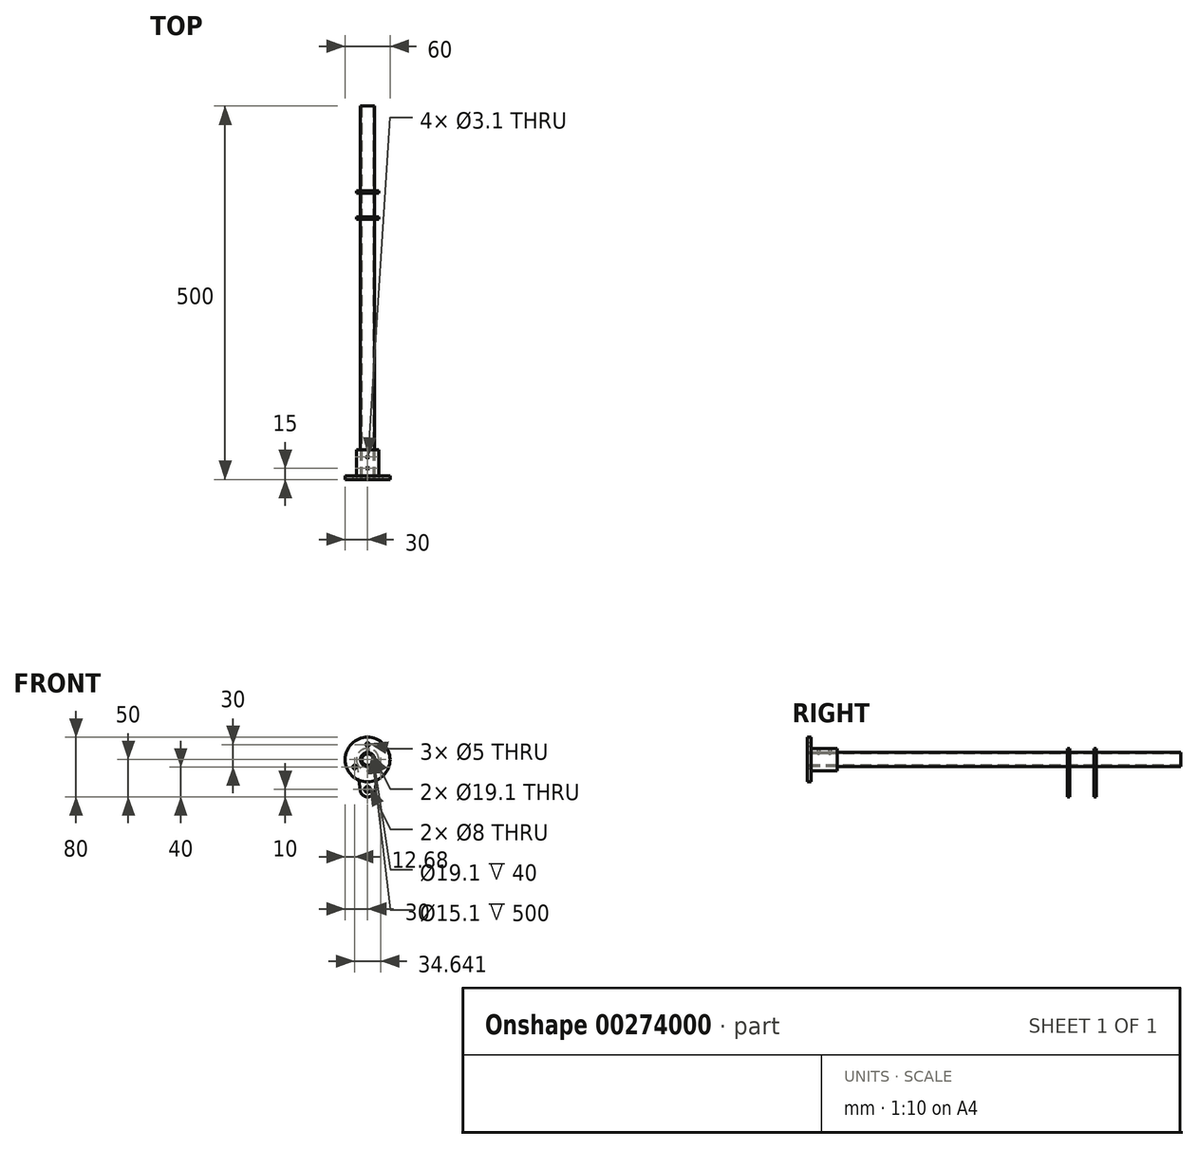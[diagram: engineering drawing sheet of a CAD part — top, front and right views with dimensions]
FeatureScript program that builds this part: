
annotation { "Feature Type Name" : "Feature", "Feature Type Description" : "" }
export const myFeature = defineFeature(function(context is Context, id is Id, definition is map)
    precondition{}
    {
        {
            var Q0;
            Q0=qCreatedBy(makeId("Front.planeOp"),FACE);
            var sketch = newSketch(context, id + "F0", { "sketchPlane" : qUnion([Q0])});
            skCircle(sketch, "E0", {"center": v(0, 0) * mm, "radius": 9.55 * mm});
            skCircle(sketch, "E1", {"center": v(0, 0) * mm, "radius": 7.55 * mm});
            skSolve(sketch);
        }
        {
            var Q0;
            Q0=qSketchRegion(id+"F0",true);
            extrude(context, id + "F1", {"entities" : qUnion([Q0]), "oppositeDirection" : true, "depth" : 500 * mm});
        }
        {
            var Q0;
            Q0=qCreatedBy(makeId("Right.planeOp"),FACE);
            var sketch = newSketch(context, id + "F2", { "sketchPlane" : qUnion([Q0])});
            skLineSegment(sketch, "E2", {"start": v(0, -9.55) * mm, "end": v(500, -9.55) * mm, "construction": true});
            skLineSegment(sketch, "E3", {"start": v(500, 9.55) * mm, "end": v(0, 9.55) * mm, "construction": true});
            skLineSegment(sketch, "E4", {"start": v(0, 9.55) * mm, "end": v(0, -9.55) * mm, "construction": true});
            skLineSegment(sketch, "E5", {"start": v(0, 0) * mm, "end": v(72.27, 0) * mm, "construction": true});
            skLineSegment(sketch, "E6", {"start": v(0, 9.55) * mm, "end": v(0, 30) * mm});
            skLineSegment(sketch, "E7", {"start": v(0, 30) * mm, "end": v(5, 30) * mm});
            skLineSegment(sketch, "E8", {"start": v(5, 30) * mm, "end": v(5, 15) * mm});
            skLineSegment(sketch, "E9", {"start": v(5, 15) * mm, "end": v(40, 15) * mm});
            skLineSegment(sketch, "E10", {"start": v(40, 15) * mm, "end": v(40, 9.55) * mm});
            skLineSegment(sketch, "E11", {"start": v(40, 9.55) * mm, "end": v(0, 9.55) * mm});
            skSolve(sketch);
        }
        {
            var Q0;
            Q0=qSketchRegion(id+"F2",true);
            var Q1;
            Q1=sQuery(id+"F2.wireOp",EDGE,"E5");
            revolve(context, id + "F3", {"entities" : qUnion([Q0]), "axis" : qUnion([Q1]), "revolveType" : RevolveType.FULL});
        }
        {
            var Q0;
            Q0=makeQuery(id+"F3.opRevolve","SWEPT_FACE",FACE,{"disambiguationData":[OSD([sQuery(id+"F2.wireOp",EDGE,"E6")])]});
            var sketch = newSketch(context, id + "F4", { "sketchPlane" : qUnion([Q0])});
            skCircle(sketch, "E12", {"center": v(0, 0) * mm, "radius": 20 * mm, "construction": true});
            skCircle(sketch, "E13", {"center": v(0, 20) * mm, "radius": 2.5 * mm});
            skCircle(sketch, "E14.1.0", {"center": v(-17.32, -10) * mm, "radius": 2.5 * mm});
            skCircle(sketch, "E14.2.0", {"center": v(17.32, -10) * mm, "radius": 2.5 * mm});
            skSolve(sketch);
        }
        {
            var Q0;
            Q0=qSketchRegion(id+"F4",true);
            extrude(context, id + "F5", {"entities" : qUnion([Q0]), "operationType" : NewBodyOperationType.REMOVE, "endBound" : BoundingType.THROUGH_ALL, "oppositeDirection" : true, "depth" : 25 * mm});
        }
        {
            var Q0;
            Q0=qCreatedBy(makeId("Top.planeOp"),FACE);
            var sketch = newSketch(context, id + "F6", { "sketchPlane" : qUnion([Q0])});
            skLineSegment(sketch, "E15", {"start": v(0, 0) * mm, "end": v(0, 30) * mm, "construction": true});
            skCircle(sketch, "E16", {"center": v(0, 30) * mm, "radius": 1.55 * mm});
            skCircle(sketch, "E17", {"center": v(0, 15) * mm, "radius": 1.55 * mm});
            skSolve(sketch);
        }
        {
            var Q0;
            Q0=qSketchRegion(id+"F6",true);
            extrude(context, id + "F7", {"entities" : qUnion([Q0]), "operationType" : NewBodyOperationType.REMOVE, "endBound" : BoundingType.THROUGH_ALL, "depth" : 25 * mm});
        }
        {
            var Q0;
            Q0=makeQuery(id+"F1.opExtrude","CAP_FACE",FACE,{"disambiguationData":[OSD([sQuery(id+"F0.wireOp",EDGE,"E0"),sQuery(id+"F0.wireOp",EDGE,"E1")])],"isStart":false});
            cPlane(context, id + "F8", {"entities" : qUnion([Q0]), "cplaneType" : CPlaneType.OFFSET, "offset" : 150 * mm, "oppositeDirection" : true, "width" : 150 * mm, "height" : 150 * mm});
        }
        {
            var Q0;
            Q0=qCreatedBy(id+"F8.planeOp",FACE);
            var sketch = newSketch(context, id + "F9", { "sketchPlane" : qUnion([Q0])});
            skCircle(sketch, "E18.0", {"center": v(0, 0) * mm, "radius": 9.55 * mm});
            skArc(sketch, "E19.0", {"start": v(14.88, -1.87) * mm, "mid": v(0, 15) * mm, "end": v(-14.88, -1.87) * mm});
            skLineSegment(sketch, "E20", {"start": v(0, 0) * mm, "end": v(0, -40) * mm, "construction": true});
            skArc(sketch, "E21", {"start": v(-9.92, -41.25) * mm, "mid": v(0, -50) * mm, "end": v(9.92, -41.25) * mm});
            skLineSegment(sketch, "E22", {"start": v(-14.88, -1.87) * mm, "end": v(-9.92, -41.25) * mm});
            skLineSegment(sketch, "E23", {"start": v(14.88, -1.87) * mm, "end": v(9.92, -41.25) * mm});
            skCircle(sketch, "E24", {"center": v(0, -40) * mm, "radius": 4 * mm});
            skSolve(sketch);
        }
        {
            var Q0;
            Q0=makeQuery(id+"F9.imprint","IMPRINT",FACE,{"disambiguationData":[TD([[makeQuery(id+"F9.imprint","IMPRINT",EDGE,{"derivedFrom":sQuery(id+"F9.wireOp",EDGE,"E18.0")}),-1.0]])]});
            extrude(context, id + "F10", {"entities" : qUnion([Q0]), "endBound" : BoundingType.SYMMETRIC, "depth" : 3.2 * mm});
        }
        {
            var Q0;
            Q0=makeQuery(id+"F10.opExtrude","SWEPT_BODY",BODY,{"disambiguationData":[OSD([sQuery(id+"F9.wireOp",EDGE,"E18.0"),sQuery(id+"F9.wireOp",EDGE,"E19.0"),sQuery(id+"F9.wireOp",EDGE,"E21"),sQuery(id+"F9.wireOp",EDGE,"E22"),sQuery(id+"F9.wireOp",EDGE,"E23"),sQuery(id+"F9.wireOp",EDGE,"E24")])]});
            transform(context, id + "F11", {"entities" : qUnion([Q0]), "transformType" : TransformType.TRANSLATION_3D, "dx" : 0 * mm, "dy" : 35 * mm, "dz" : 0 * mm, "makeCopy" : true});
        }
    });
